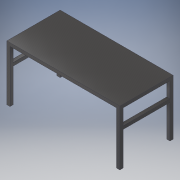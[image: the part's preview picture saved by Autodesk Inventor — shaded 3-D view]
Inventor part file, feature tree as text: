
AUTODESK INVENTOR PART (.ipt)
format: ipt  version: 2017 (Build 210142000, 142)  size: 143,872 bytes
history: native  units: in
note: dims shown in document units (in); Inventor stores cm internally (conversion verified against a paired STEP export)
features: extrude x4, sketch x4
ambient origin geometry x8: Origin, YZ Plane, XZ Plane, XY Plane, X Axis, Y Axis, Z Axis, Center Point
bodies: Solid1 (feature_tree)
feature tree (8):
  extrude  "Extrusion1"  Depth=55.9055in
  extrude  "Extrusion2"  Depth=16.5354in
  extrude  "Extrusion3"  Depth=1.5748in
  extrude  "Extrusion4"  Depth=1.5748in
  sketch  "Sketch1"  dims[d0=27.3622in d1=55.9055in]
  sketch  "Sketch2"  dims[d2=26.378in d3=0.0in d4=16.5354in]
  sketch  "Sketch3"  dims[d5=1.5748in d6=1.5748in]
  sketch  "Sketch4"  dims[d7=78.7402in d8=0.0in d9=1.5748in d10=1.5748in d11=1.5748in d12=1.5748in d13=78.7402in d14=0.0in d15=1.5748in d16=1.5748in d17=1.5748in d18=39.3701in d19=0.0in]
